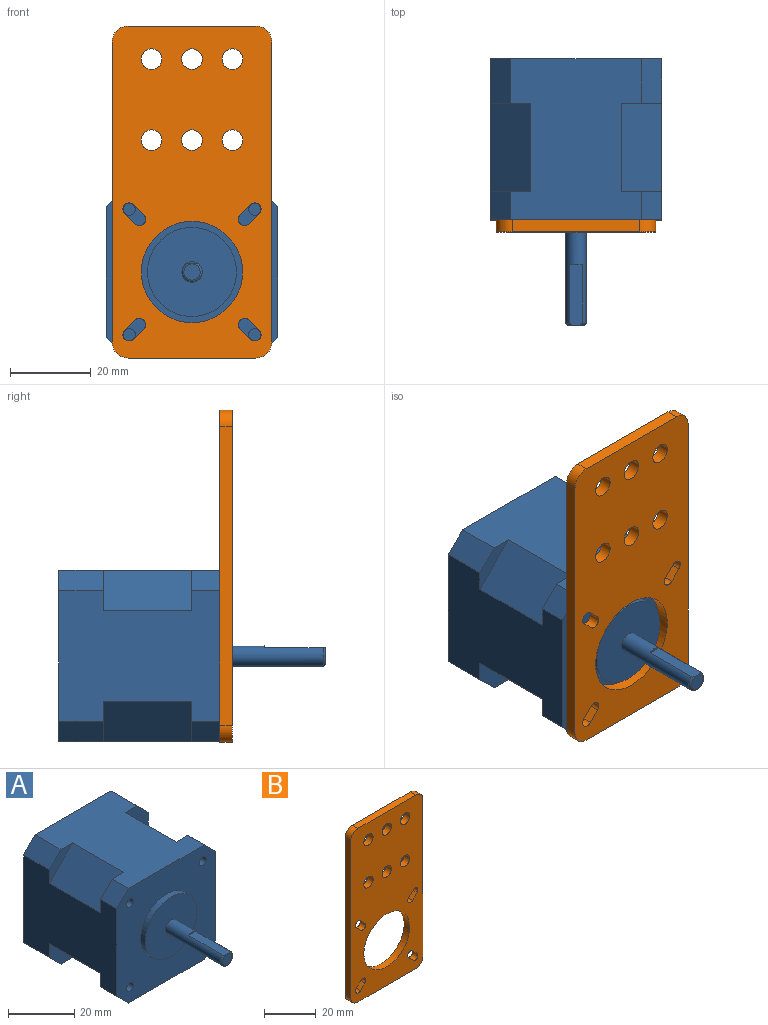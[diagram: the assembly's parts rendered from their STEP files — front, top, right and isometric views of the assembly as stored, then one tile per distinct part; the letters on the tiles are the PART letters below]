
ASSEMBLY  parts=2 mates=1
PART A: 49 faces, bbox 42.3x65.8x42.3 mm
  f0: plane 10x10mm, normal (0,-1,0), area 37.5mm2, adj f4,f5,f10,f21
  f1: plane 10x10mm, normal (0,-1,0), area 37.5mm2, adj f5,f6,f9,f22
  f2: plane 10x10mm, normal (0,-1,0), area 37.5mm2, adj f3,f6,f12,f23
  f3: plane 39.8x32.3mm, normal (1,0,0), area 1067.5mm2, adj f2,f7,f8,f11,f12,f23,f24,f26
  f4: plane 39.8x32.3mm, normal (0,0,-1), area 1067.5mm2, adj f0,f7,f8,f10,f11,f21,f24,f25
  f5: plane 39.8x32.3mm, normal (-1,0,0), area 1067.5mm2, adj f0,f1,f7,f9,f10,f21,f22,f25
  f6: plane 39.8x32.3mm, normal (0,0,1), area 1067.5mm2, adj f1,f2,f7,f9,f12,f22,f23,f27
  f7: plane 42.3x42.3mm, normal (0,1,0), area 1711mm2, adj f3,f4,f5,f6,f9,f10,f11,f12
  f8: plane 10x10mm, normal (0,-1,0), area 37.5mm2, adj f3,f4,f11,f24
  f9: plane 11x5mm, normal (-0.71,0,0.71), area 77.8mm2, adj f1,f5,f6,f7
  f10: plane 11x5mm, normal (-0.71,0,-0.71), area 77.8mm2, adj f0,f4,f5,f7
  f11: plane 11x5mm, normal (0.71,0,-0.71), area 77.8mm2, adj f3,f4,f7,f8
  f12: plane 11x5mm, normal (0.71,0,0.71), area 77.8mm2, adj f2,f3,f6,f7
  f13: cylinder r=1.5mm len=4.5mm, axis (0,1,0), area 42.4mm2, adj f7,f14
  f14: plane 3x3mm, normal (0,1,0), area 7.1mm2, adj f13
  f15: cylinder r=1.5mm len=4.5mm, axis (0,1,0), area 42.4mm2, adj f7,f16
  f16: plane 3x3mm, normal (0,1,0), area 7.1mm2, adj f15
  f17: cylinder r=1.5mm len=4.5mm, axis (0,1,0), area 42.4mm2, adj f7,f18
  f18: plane 3x3mm, normal (0,1,0), area 7.1mm2, adj f17
  f19: cylinder r=1.5mm len=4.5mm, axis (0,1,0), area 42.4mm2, adj f7,f20
  f20: plane 3x3mm, normal (0,1,0), area 7.1mm2, adj f19
  f21: plane 21.8x10mm, normal (-0.71,0,-0.71), area 308.3mm2, adj f0,f4,f5,f25
  f22: plane 21.8x10mm, normal (-0.71,0,0.71), area 308.3mm2, adj f1,f5,f6,f28
  f23: plane 21.8x10mm, normal (0.71,0,0.71), area 308.3mm2, adj f2,f3,f6,f27
  f24: plane 21.8x10mm, normal (0.71,0,-0.71), area 308.3mm2, adj f3,f4,f8,f26
  f25: plane 10x10mm, normal (0,1,0), area 37.5mm2, adj f4,f5,f21,f35
  f26: plane 10x10mm, normal (0,1,0), area 37.5mm2, adj f3,f4,f24,f36
  f27: plane 10x10mm, normal (0,1,0), area 37.5mm2, adj f3,f6,f23,f37
  f28: plane 10x10mm, normal (0,1,0), area 37.5mm2, adj f5,f6,f22,f38
  f29: cylinder r=2.5mm len=23.5mm, axis (0,1,0), area 322.5mm2, adj f31,f32,f33,f40
  f30: plane 4x4mm, normal (0,-1,0), area 12.6mm2, adj f33
  f31: plane 15x3mm, normal (0,0,1), area 44.8mm2, adj f29,f32,f33
  f32: plane 3x0.5mm, normal (0,-1,0), area 1mm2, adj f29,f31
  f33: torus R=2mm, axis (0,-1,0), area 9.6mm2, adj f29,f30,f31
  f34: plane 42.3x42.3mm, normal (0,-1,0), area 1330.9mm2, adj f3,f4,f5,f6,f35,f36,f37,f38
  f35: plane 7x5mm, normal (-0.71,0,-0.71), area 49.5mm2, adj f4,f5,f25,f34
  f36: plane 7x5mm, normal (0.71,0,-0.71), area 49.5mm2, adj f3,f4,f26,f34
  f37: plane 7x5mm, normal (0.71,0,0.71), area 49.5mm2, adj f3,f6,f27,f34
  f38: plane 7x5mm, normal (-0.71,0,0.71), area 49.5mm2, adj f5,f6,f28,f34
  f39: cylinder r=11mm len=22mm, axis (0,1,0), area 138.2mm2, adj f34,f40
  f40: plane 22x22mm, normal (0,-1,0), area 360.5mm2, adj f29,f39
  f41: cylinder r=1.5mm len=4.5mm, axis (0,-1,0), area 42.4mm2, adj f34,f42
  f42: plane 3x3mm, normal (0,-1,0), area 7.1mm2, adj f41
  f43: cylinder r=1.5mm len=4.5mm, axis (0,-1,0), area 42.4mm2, adj f34,f44
  f44: plane 3x3mm, normal (0,-1,0), area 7.1mm2, adj f43
  f45: cylinder r=1.5mm len=4.5mm, axis (0,-1,0), area 42.4mm2, adj f34,f46
  f46: plane 3x3mm, normal (0,-1,0), area 7.1mm2, adj f45
  f47: cylinder r=1.5mm len=4.5mm, axis (0,-1,0), area 42.4mm2, adj f34,f48
  f48: plane 3x3mm, normal (0,-1,0), area 7.1mm2, adj f47
PART B: 33 faces, bbox 39.5x3x82 mm
  f0: cylinder r=4mm len=4mm, axis (0,-1,0), area 18.8mm2, adj f1,f7,f29,f30
  f1: plane 74x3mm, normal (-1,0,0), area 222mm2, adj f0,f2,f29,f30
  f2: cylinder r=4mm len=4mm, axis (0,-1,0), area 18.8mm2, adj f1,f3,f29,f30
  f3: plane 31.5x3mm, normal (0,0,-1), area 94.5mm2, adj f2,f4,f29,f30
  f4: cylinder r=4mm len=4mm, axis (0,-1,0), area 18.8mm2, adj f3,f5,f29,f30
  f5: plane 74x3mm, normal (1,0,0), area 222mm2, adj f4,f6,f29,f30
  f6: cylinder r=4mm len=4mm, axis (0,-1,0), area 18.8mm2, adj f5,f7,f29,f30
  f7: plane 31.5x3mm, normal (0,0,1), area 94.5mm2, adj f0,f6,f29,f30
  f8: plane 3x2.5mm, normal (-0.71,0,-0.71), area 10.6mm2, adj f9,f11,f29,f30
  f9: cylinder r=1.55mm len=3mm, axis (0,-1,0), area 14.6mm2, adj f8,f10,f29,f30
  f10: plane 3x2.5mm, normal (0.71,0,0.71), area 10.6mm2, adj f9,f11,f29,f30
  f11: cylinder r=1.55mm len=3mm, axis (0,-1,0), area 14.6mm2, adj f8,f10,f29,f30
  f12: cylinder r=2.55mm len=5.1mm, axis (0,-1,0), area 48.1mm2, adj f29,f30
  f13: cylinder r=2.55mm len=5.1mm, axis (0,-1,0), area 48.1mm2, adj f29,f30
  f14: cylinder r=2.55mm len=5.1mm, axis (0,-1,0), area 48.1mm2, adj f29,f30
  f15: plane 3x2.5mm, normal (0.71,0,0.71), area 10.6mm2, adj f16,f18,f29,f30
  f16: cylinder r=1.55mm len=3mm, axis (0,-1,0), area 14.6mm2, adj f15,f17,f29,f30
  f17: plane 3x2.5mm, normal (-0.71,0,-0.71), area 10.6mm2, adj f16,f18,f29,f30
  f18: cylinder r=1.55mm len=3mm, axis (0,-1,0), area 14.6mm2, adj f15,f17,f29,f30
  f19: cylinder r=12.5mm len=25mm, axis (0,-1,0), area 235.6mm2, adj f29,f30
  f20: cylinder r=2.55mm len=5.1mm, axis (0,-1,0), area 48.1mm2, adj f29,f30
  f21: cylinder r=2.55mm len=5.1mm, axis (0,-1,0), area 48.1mm2, adj f29,f30
  f22: cylinder r=2.55mm len=5.1mm, axis (0,-1,0), area 48.1mm2, adj f29,f30
  f23: plane 3x2.5mm, normal (0.71,0,-0.71), area 10.6mm2, adj f24,f26,f29,f30
  f24: cylinder r=1.55mm len=3mm, axis (0,-1,0), area 14.6mm2, adj f23,f25,f29,f30
  f25: plane 3x2.5mm, normal (-0.71,0,0.71), area 10.6mm2, adj f24,f26,f29,f30
  f26: cylinder r=1.55mm len=3mm, axis (0,-1,0), area 14.6mm2, adj f23,f25,f29,f30
  f27: plane 3x2.5mm, normal (0.71,0,-0.71), area 10.6mm2, adj f28,f29,f30,f32
  f28: cylinder r=1.55mm len=3mm, axis (0,-1,0), area 14.6mm2, adj f27,f29,f30,f31
  f29: plane 82x39.5mm, normal (0,1,0), area 2537.8mm2, adj f0,f1,f2,f3,f4,f5,f6,f7
  f30: plane 82x39.5mm, normal (0,-1,0), area 2537.8mm2, adj f0,f1,f2,f3,f4,f5,f6,f7
  f31: plane 3x2.5mm, normal (-0.71,0,0.71), area 10.6mm2, adj f28,f29,f30,f32
  f32: cylinder r=1.55mm len=3mm, axis (0,-1,0), area 14.6mm2, adj f27,f29,f30,f31
PLACE A t=(4.26,-5.9,20.16)mm fixed
PLACE B rot(axis=(0,1,0),0deg) t=(4.26,-6.9,20.16)mm
MATE fastened A.f19 <-> B.f18  axis (0,-1,0) through (19.76,-3.9,4.66)mm
